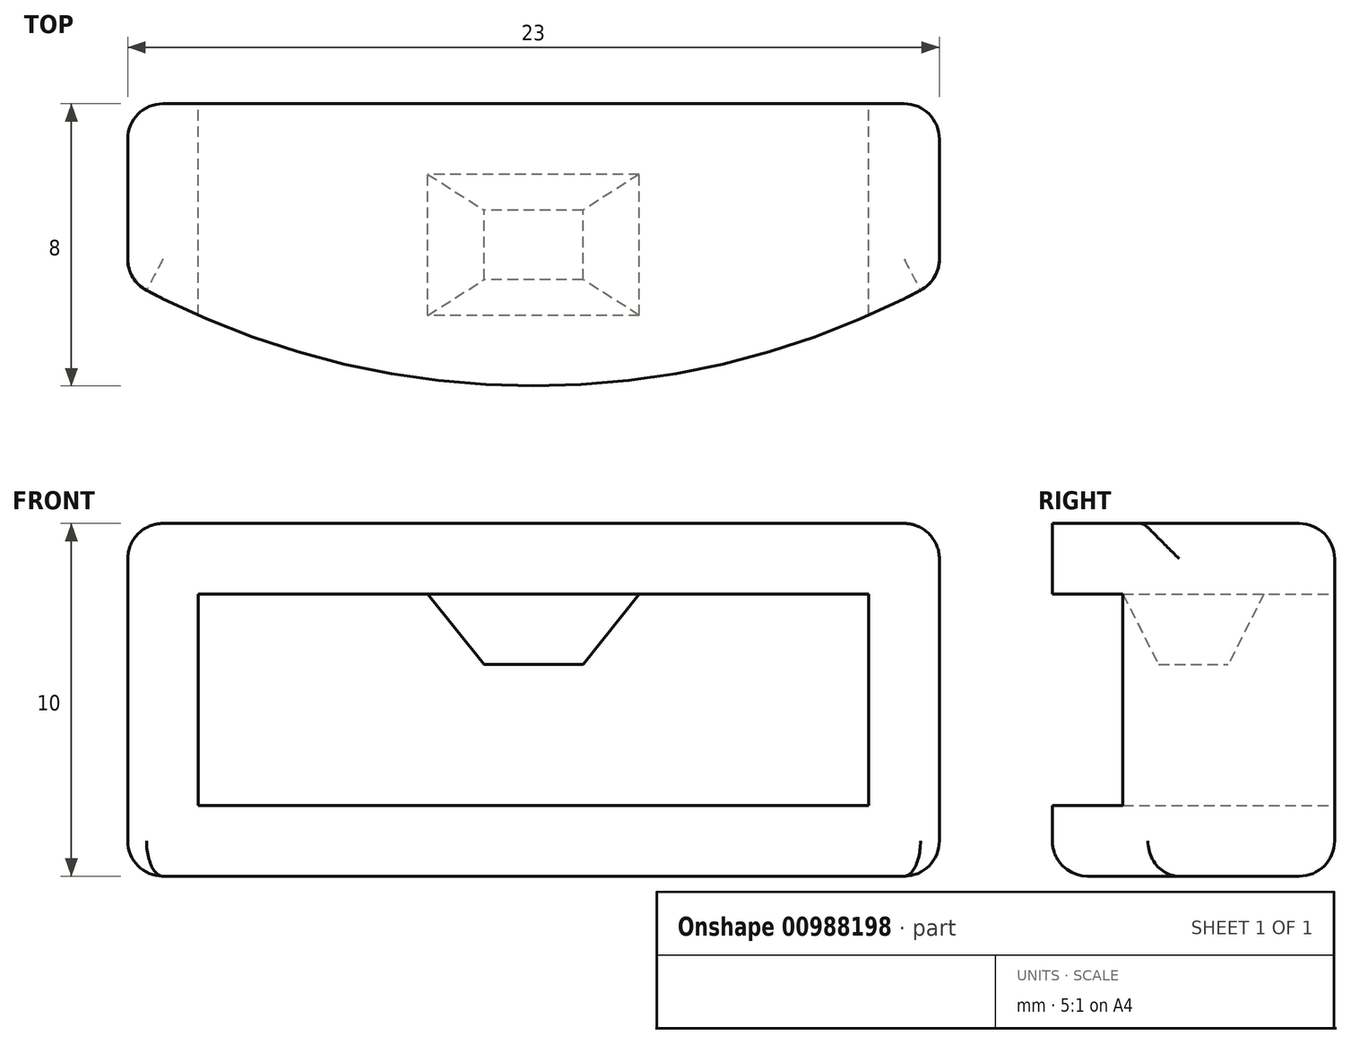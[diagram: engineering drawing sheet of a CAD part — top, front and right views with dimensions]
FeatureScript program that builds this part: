
annotation { "Feature Type Name" : "Feature", "Feature Type Description" : "" }
export const myFeature = defineFeature(function(context is Context, id is Id, definition is map)
    precondition{}
    {
        {
            var Q0;
            Q0=qCreatedBy(makeId("Front.planeOp"),FACE);
            var sketch = newSketch(context, id + "F0", { "sketchPlane" : qUnion([Q0])});
            skLineSegment(sketch, "E0.bottom", {"start": v(11.5, 5) * mm, "end": v(-11.5, 5) * mm});
            skLineSegment(sketch, "E0.top", {"start": v(11.5, -5) * mm, "end": v(-11.5, -5) * mm});
            skLineSegment(sketch, "E0.left", {"start": v(11.5, 5) * mm, "end": v(11.5, -5) * mm});
            skLineSegment(sketch, "E0.right", {"start": v(-11.5, 5) * mm, "end": v(-11.5, -5) * mm});
            skPoint(sketch, "E0.middle", {"position": v(0, 0) * mm});
            skSolve(sketch);
        }
        {
            var Q0;
            Q0=makeQuery(id+"F0.imprint","IMPRINT",FACE,{"disambiguationData":[TD([[makeQuery(id+"F0.imprint","IMPRINT",EDGE,{"derivedFrom":sQuery(id+"F0.wireOp",EDGE,"E0.bottom")}),1.0]])]});
            extrude(context, id + "F1", {"entities" : qUnion([Q0]), "depth" : 8 * mm, "offsetDistance" : 25 * mm, "symmetric" : true});
        }
        {
            var Q0;
            Q0=makeQuery(id+"F1.opExtrude","SWEPT_FACE",FACE,{"disambiguationData":[OSD([sQuery(id+"F0.wireOp",EDGE,"E0.bottom")])]});
            var sketch = newSketch(context, id + "F2", { "sketchPlane" : qUnion([Q0])});
            skArc(sketch, "E1", {"start": v(-11.5, -1) * mm, "mid": v(0, -4) * mm, "end": v(11.5, -1) * mm});
            skPoint(sketch, "E2", {"position": v(0, -4) * mm});
            skSolve(sketch);
        }
        {
            var Q0;
            {var subQ0=sQuery(id+"F2.wireOp",EDGE,"E1");var subQ1=sQuery(id+"F0.wireOp",EDGE,"E0.bottom");var subQ4=makeQuery(id+"F1.opExtrude","CAP_EDGE",EDGE,{"disambiguationData":[OSD([subQ1])],"isStart":false});var subQ5=makeQuery(id+"F2.imprint","INTERSECT",VERTEX,{"derivedFrom":[subQ4,subQ0]});Q0=makeQuery(id+"F2.imprint","IMPRINT",FACE,{"disambiguationData":[TD([[makeQuery(id+"F2.imprint","IMPRINT",EDGE,{"disambiguationData":[TD([[subQ5,1.0]])],"derivedFrom":subQ0}),-1.0]])]});}
            var Q1;
            {var subQ0=sQuery(id+"F2.wireOp",EDGE,"E1");var subQ1=sQuery(id+"F0.wireOp",EDGE,"E0.bottom");var subQ4=makeQuery(id+"F1.opExtrude","CAP_EDGE",EDGE,{"disambiguationData":[OSD([subQ1])],"isStart":false});var subQ5=makeQuery(id+"F2.imprint","INTERSECT",VERTEX,{"derivedFrom":[subQ4,subQ0]});Q1=makeQuery(id+"F2.imprint","IMPRINT",FACE,{"disambiguationData":[TD([[makeQuery(id+"F2.imprint","IMPRINT",EDGE,{"disambiguationData":[TD([[subQ5,-1.0]])],"derivedFrom":subQ0}),-1.0]])]});}
            extrude(context, id + "F3", {"entities" : qUnion([Q0, Q1]), "operationType" : NewBodyOperationType.REMOVE, "endBound" : BoundingType.THROUGH_ALL, "oppositeDirection" : true, "depth" : 25 * mm, "offsetDistance" : 25 * mm});
        }
        {
            var Q0;
            Q0=makeQuery(id+"F1.opExtrude","CAP_FACE",FACE,{"disambiguationData":[OSD([sQuery(id+"F0.wireOp",EDGE,"E0.bottom"),sQuery(id+"F0.wireOp",EDGE,"E0.top"),sQuery(id+"F0.wireOp",EDGE,"E0.left"),sQuery(id+"F0.wireOp",EDGE,"E0.right")])],"isStart":true});
            var sketch = newSketch(context, id + "F4", { "sketchPlane" : qUnion([Q0])});
            skLineSegment(sketch, "E3.0", {"start": v(-9.5, 3) * mm, "end": v(9.5, 3) * mm});
            skLineSegment(sketch, "E4.0", {"start": v(9.5, 3) * mm, "end": v(9.5, -3) * mm});
            skLineSegment(sketch, "E4.1", {"start": v(-9.5, -3) * mm, "end": v(9.5, -3) * mm});
            skLineSegment(sketch, "E4.2", {"start": v(-9.5, 3) * mm, "end": v(-9.5, -3) * mm});
            skSolve(sketch);
        }
        {
            var Q0;
            Q0=makeQuery(id+"F4.imprint","IMPRINT",FACE,{"disambiguationData":[TD([[makeQuery(id+"F4.imprint","IMPRINT",EDGE,{"derivedFrom":sQuery(id+"F4.wireOp",EDGE,"E3.0")}),-1.0]])]});
            extrude(context, id + "F5", {"entities" : qUnion([Q0]), "operationType" : NewBodyOperationType.REMOVE, "endBound" : BoundingType.THROUGH_ALL, "oppositeDirection" : true, "depth" : 25 * mm, "offsetDistance" : 25 * mm});
        }
        {
            var Q0;
            Q0=makeQuery(id+"F5.boolean.opBoolean","COPY",FACE,{"derivedFrom":makeQuery(id+"F5.opExtrude","SWEPT_FACE",FACE,{"disambiguationData":[OSD([sQuery(id+"F4.wireOp",EDGE,"E3.0")])]})});
            var sketch = newSketch(context, id + "F6", { "sketchPlane" : qUnion([Q0])});
            skLineSegment(sketch, "E5.bottom", {"start": v(3, 2) * mm, "end": v(-3, 2) * mm});
            skLineSegment(sketch, "E5.top", {"start": v(3, -2) * mm, "end": v(-3, -2) * mm});
            skLineSegment(sketch, "E5.left", {"start": v(3, 2) * mm, "end": v(3, -2) * mm});
            skLineSegment(sketch, "E5.right", {"start": v(-3, 2) * mm, "end": v(-3, -2) * mm});
            skPoint(sketch, "E5.middle", {"position": v(0, 0) * mm});
            skSolve(sketch);
        }
        {
            var Q0;
            Q0=makeQuery(id+"F6.imprint","IMPRINT",FACE,{"disambiguationData":[TD([[makeQuery(id+"F6.imprint","IMPRINT",EDGE,{"derivedFrom":sQuery(id+"F6.wireOp",EDGE,"E5.bottom")}),1.0]])]});
            cPlane(context, id + "F7", {"entities" : qUnion([Q0]), "cplaneType" : CPlaneType.OFFSET, "offset" : 2 * mm, "width" : 150 * mm, "height" : 150 * mm});
        }
        {
            var Q0;
            Q0=qCreatedBy(id+"F7.planeOp",FACE);
            var sketch = newSketch(context, id + "F8", { "sketchPlane" : qUnion([Q0])});
            skLineSegment(sketch, "E6.bottom", {"start": v(1.4, 0.99) * mm, "end": v(-1.4, 0.99) * mm});
            skLineSegment(sketch, "E6.top", {"start": v(1.4, -0.99) * mm, "end": v(-1.4, -0.99) * mm});
            skLineSegment(sketch, "E6.left", {"start": v(1.4, 0.99) * mm, "end": v(1.4, -0.99) * mm});
            skLineSegment(sketch, "E6.right", {"start": v(-1.4, 0.99) * mm, "end": v(-1.4, -0.99) * mm});
            skPoint(sketch, "E6.middle", {"position": v(0, 0) * mm});
            skSolve(sketch);
        }
        {
            var Q1;
            Q1=makeQuery(id+"F6.imprint","IMPRINT",FACE,{"disambiguationData":[TD([[makeQuery(id+"F6.imprint","IMPRINT",EDGE,{"derivedFrom":sQuery(id+"F6.wireOp",EDGE,"E5.bottom")}),1.0]])]});
            var Q2;
            Q2=makeQuery(id+"F8.imprint","IMPRINT",FACE,{"disambiguationData":[TD([[makeQuery(id+"F8.imprint","IMPRINT",EDGE,{"derivedFrom":sQuery(id+"F8.wireOp",EDGE,"E6.bottom")}),1.0]])]});
            loft(context, id + "F9", {"operationType" : NewBodyOperationType.ADD, "sheetProfilesArray" : [{ "sheetProfileEntities" : qUnion([Q1]) }, { "sheetProfileEntities" : qUnion([Q2]) }]});
        }
        {
            var Q0;
            Q0=makeQuery(id+"F1.opExtrude","CAP_EDGE",EDGE,{"disambiguationData":[OSD([sQuery(id+"F0.wireOp",EDGE,"E0.top")])],"isStart":true});
            var Q1;
            Q1=makeQuery(id+"F1.opExtrude","CAP_EDGE",EDGE,{"disambiguationData":[OSD([sQuery(id+"F0.wireOp",EDGE,"E0.right")])],"isStart":true});
            var Q2;
            Q2=makeQuery(id+"F1.opExtrude","CAP_EDGE",EDGE,{"disambiguationData":[OSD([sQuery(id+"F0.wireOp",EDGE,"E0.bottom")])],"isStart":true});
            var Q3;
            Q3=makeQuery(id+"F1.opExtrude","CAP_EDGE",EDGE,{"disambiguationData":[OSD([sQuery(id+"F0.wireOp",EDGE,"E0.left")])],"isStart":true});
            var Q4;
            Q4=makeQuery(id+"F3.boolean.opBoolean","COPY",EDGE,{"derivedFrom":makeQuery(id+"F3.opExtrude","SWEPT_EDGE",EDGE,{"disambiguationData":[OSD([sQuery(id+"F0.wireOp",EDGE,"E0.bottom"),sQuery(id+"F0.wireOp",EDGE,"E0.left"),sQuery(id+"F2.wireOp",EDGE,"E1")])]})});
            var Q5;
            {var subQ0=sQuery(id+"F2.wireOp",EDGE,"E1");var subQ1=sQuery(id+"F0.wireOp",EDGE,"E0.bottom");var subQ2=makeQuery(id+"F2.imprint","INTERSECT",VERTEX,{"derivedFrom":[makeQuery(id+"F1.opExtrude","CAP_EDGE",EDGE,{"disambiguationData":[OSD([subQ1])],"isStart":false}),subQ0]});Q5=makeQuery(id+"F3.boolean.opBoolean","INTERSECT",EDGE,{"derivedFrom":[makeQuery(id+"F1.opExtrude","SWEPT_FACE",FACE,{"disambiguationData":[OSD([sQuery(id+"F0.wireOp",EDGE,"E0.top")])]}),makeQuery(id+"F3.opExtrude","SWEPT_FACE",FACE,{"disambiguationData":[OSD([subQ0]),TDD([makeQuery(id+"F2.imprint","IMPRINT",EDGE,{"disambiguationData":[TD([[subQ2,1.0]])],"derivedFrom":subQ0})])]}),makeQuery(id+"F3.opExtrude","SWEPT_FACE",FACE,{"disambiguationData":[OSD([subQ0]),TDD([makeQuery(id+"F2.imprint","IMPRINT",EDGE,{"disambiguationData":[TD([[subQ2,-1.0]])],"derivedFrom":subQ0})])]})]});}
            var Q6;
            Q6=makeQuery(id+"F3.boolean.opBoolean","COPY",EDGE,{"derivedFrom":makeQuery(id+"F3.opExtrude","SWEPT_EDGE",EDGE,{"disambiguationData":[OSD([sQuery(id+"F0.wireOp",EDGE,"E0.bottom"),sQuery(id+"F0.wireOp",EDGE,"E0.right"),sQuery(id+"F2.wireOp",EDGE,"E1")])]})});
            var Q7;
            {var subQ0=sQuery(id+"F2.wireOp",EDGE,"E1");var subQ1=sQuery(id+"F0.wireOp",EDGE,"E0.bottom");var subQ2=makeQuery(id+"F2.imprint","INTERSECT",VERTEX,{"derivedFrom":[makeQuery(id+"F1.opExtrude","CAP_EDGE",EDGE,{"disambiguationData":[OSD([subQ1])],"isStart":false}),subQ0]});Q7=makeQuery(id+"F3.boolean.opBoolean","MERGE",EDGE,{"derivedFrom":[],"fromTools":[makeQuery(id+"F3.opExtrude","CAP_EDGE",EDGE,{"disambiguationData":[OSD([subQ0]),TDD([makeQuery(id+"F2.imprint","IMPRINT",EDGE,{"disambiguationData":[TD([[subQ2,1.0]])],"derivedFrom":subQ0})])],"isStart":true}),makeQuery(id+"F3.opExtrude","CAP_EDGE",EDGE,{"disambiguationData":[OSD([subQ0]),TDD([makeQuery(id+"F2.imprint","IMPRINT",EDGE,{"disambiguationData":[TD([[subQ2,-1.0]])],"derivedFrom":subQ0})])],"isStart":true})]});}
            fillet(context, id + "F10", {"entities" : qUnion([Q0, Q1, Q2, Q3, Q4, Q5, Q6, Q7]), "radius" : 1 * mm, "tangentPropagation" : true, "allowEdgeOverflow" : false});
        }
        {
            var Q0;
            Q0=makeQuery(id+"F1.opExtrude","SWEPT_EDGE",EDGE,{"disambiguationData":[OSD([sQuery(id+"F0.wireOp",EDGE,"E0.top"),sQuery(id+"F0.wireOp",EDGE,"E0.left")])]});
            var Q1;
            Q1=makeQuery(id+"F1.opExtrude","SWEPT_EDGE",EDGE,{"disambiguationData":[OSD([sQuery(id+"F0.wireOp",EDGE,"E0.top"),sQuery(id+"F0.wireOp",EDGE,"E0.right")])]});
            var Q2;
            Q2=makeQuery(id+"F1.opExtrude","SWEPT_EDGE",EDGE,{"disambiguationData":[OSD([sQuery(id+"F0.wireOp",EDGE,"E0.bottom"),sQuery(id+"F0.wireOp",EDGE,"E0.left")])]});
            var Q3;
            Q3=makeQuery(id+"F1.opExtrude","SWEPT_EDGE",EDGE,{"disambiguationData":[OSD([sQuery(id+"F0.wireOp",EDGE,"E0.bottom"),sQuery(id+"F0.wireOp",EDGE,"E0.right")])]});
            fillet(context, id + "F11", {"entities" : qUnion([Q0, Q1, Q2, Q3]), "radius" : 1 * mm, "tangentPropagation" : true, "allowEdgeOverflow" : false});
        }
    });
